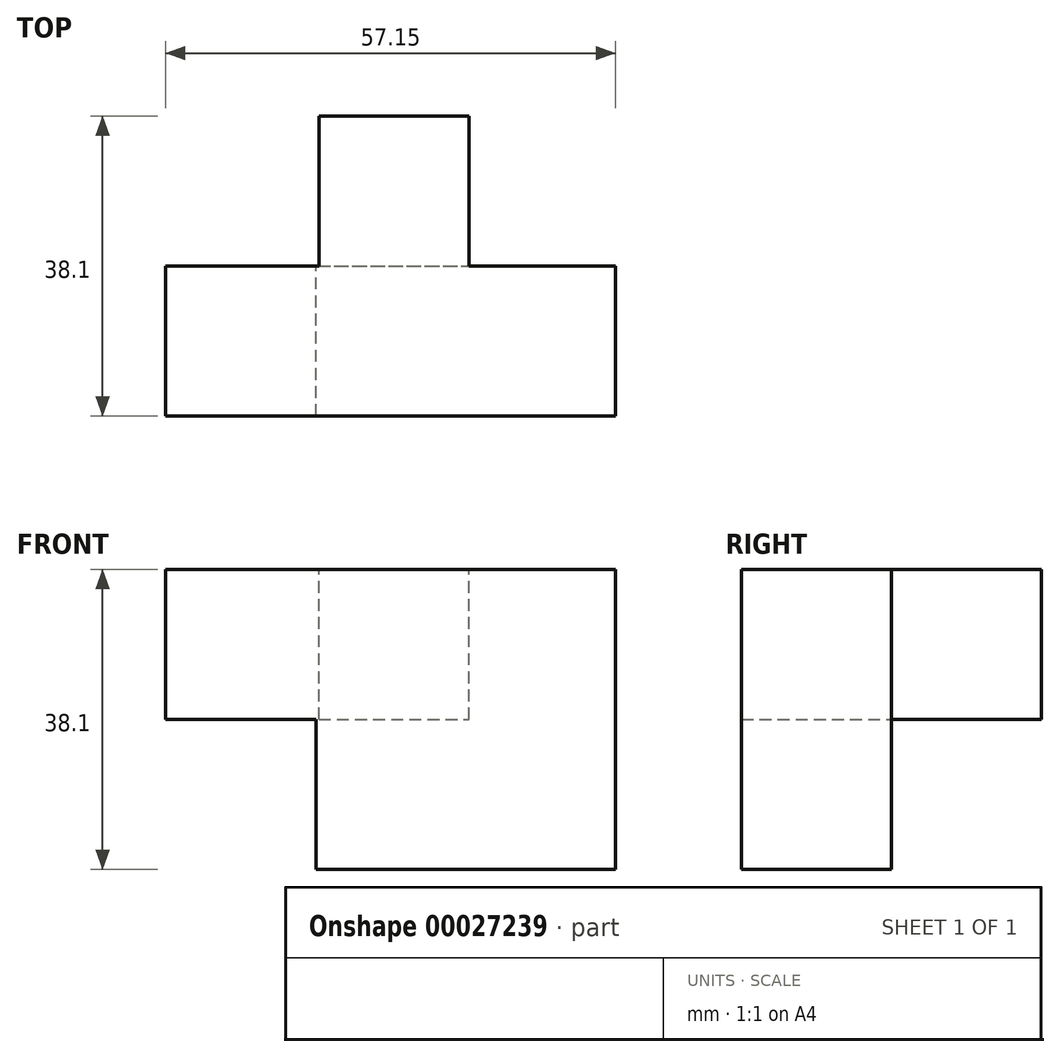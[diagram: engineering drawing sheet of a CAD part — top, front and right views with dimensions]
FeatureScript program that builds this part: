
annotation { "Feature Type Name" : "Feature", "Feature Type Description" : "" }
export const myFeature = defineFeature(function(context is Context, id is Id, definition is map)
    precondition{}
    {
        {
            var Q0;
            Q0=qCreatedBy(makeId("Top.planeOp"),FACE);
            var sketch = newSketch(context, id + "F0", { "sketchPlane" : qUnion([Q0])});
            skLineSegment(sketch, "E0.bottom", {"start": v(-57.15, 19.05) * mm, "end": v(0, 19.05) * mm});
            skLineSegment(sketch, "E0.top", {"start": v(-57.15, 0) * mm, "end": v(0, 0) * mm});
            skLineSegment(sketch, "E0.left", {"start": v(-57.15, 19.05) * mm, "end": v(-57.15, 0) * mm});
            skLineSegment(sketch, "E0.right", {"start": v(0, 19.05) * mm, "end": v(0, 0) * mm});
            skSolve(sketch);
        }
        {
            var Q0;
            Q0=makeQuery(id+"F0.imprint","IMPRINT",FACE,{"disambiguationData":[TD([[makeQuery(id+"F0.imprint","IMPRINT",EDGE,{"derivedFrom":sQuery(id+"F0.wireOp",EDGE,"E0.bottom")}),-1.0]])]});
            extrude(context, id + "F1", {"entities" : qUnion([Q0]), "depth" : 19.05 * mm});
        }
        {
            var Q0;
            Q0=makeQuery(id+"F1.opExtrude","SWEPT_FACE",FACE,{"disambiguationData":[OSD([sQuery(id+"F0.wireOp",EDGE,"E0.bottom")])]});
            var sketch = newSketch(context, id + "F2", { "sketchPlane" : qUnion([Q0])});
            skLineSegment(sketch, "E1.bottom", {"start": v(37.68, 0) * mm, "end": v(18.63, 0) * mm});
            skLineSegment(sketch, "E1.top", {"start": v(37.68, 19.05) * mm, "end": v(18.63, 19.05) * mm});
            skLineSegment(sketch, "E1.left", {"start": v(37.68, 0) * mm, "end": v(37.68, 19.05) * mm});
            skLineSegment(sketch, "E1.right", {"start": v(18.63, 0) * mm, "end": v(18.63, 19.05) * mm});
            skSolve(sketch);
        }
        {
            var Q0;
            Q0 = qSketchRegion(id + "F2", true);
            extrude(context, id + "F3", {"entities" : qUnion([Q0]), "operationType" : NewBodyOperationType.ADD, "depth" : 19.05 * mm});
        }
        {
            var Q0;
            Q0=makeQuery(id+"F3.boolean.opBoolean","MERGE",FACE,{"derivedFrom":[makeQuery(id+"F1.opExtrude","CAP_FACE",FACE,{"disambiguationData":[OSD([sQuery(id+"F0.wireOp",EDGE,"E0.bottom"),sQuery(id+"F0.wireOp",EDGE,"E0.top"),sQuery(id+"F0.wireOp",EDGE,"E0.left"),sQuery(id+"F0.wireOp",EDGE,"E0.right")])],"isStart":true}),makeQuery(id+"F3.opExtrude","SWEPT_FACE",FACE,{"disambiguationData":[OSD([sQuery(id+"F2.wireOp",EDGE,"E1.bottom")])]})]});
            var sketch = newSketch(context, id + "F4", { "sketchPlane" : qUnion([Q0])});
            skLineSegment(sketch, "E2.bottom", {"start": v(-38.04, 0) * mm, "end": v(0, 0) * mm});
            skLineSegment(sketch, "E2.top", {"start": v(-38.04, -19.05) * mm, "end": v(0, -19.05) * mm});
            skLineSegment(sketch, "E2.left", {"start": v(-38.04, 0) * mm, "end": v(-38.04, -19.05) * mm});
            skLineSegment(sketch, "E2.right", {"start": v(0, 0) * mm, "end": v(0, -19.05) * mm});
            skSolve(sketch);
        }
        {
            var Q0;
            Q0 = qSketchRegion(id + "F4", true);
            extrude(context, id + "F5", {"entities" : qUnion([Q0]), "operationType" : NewBodyOperationType.ADD, "depth" : 19.05 * mm});
        }
    });
